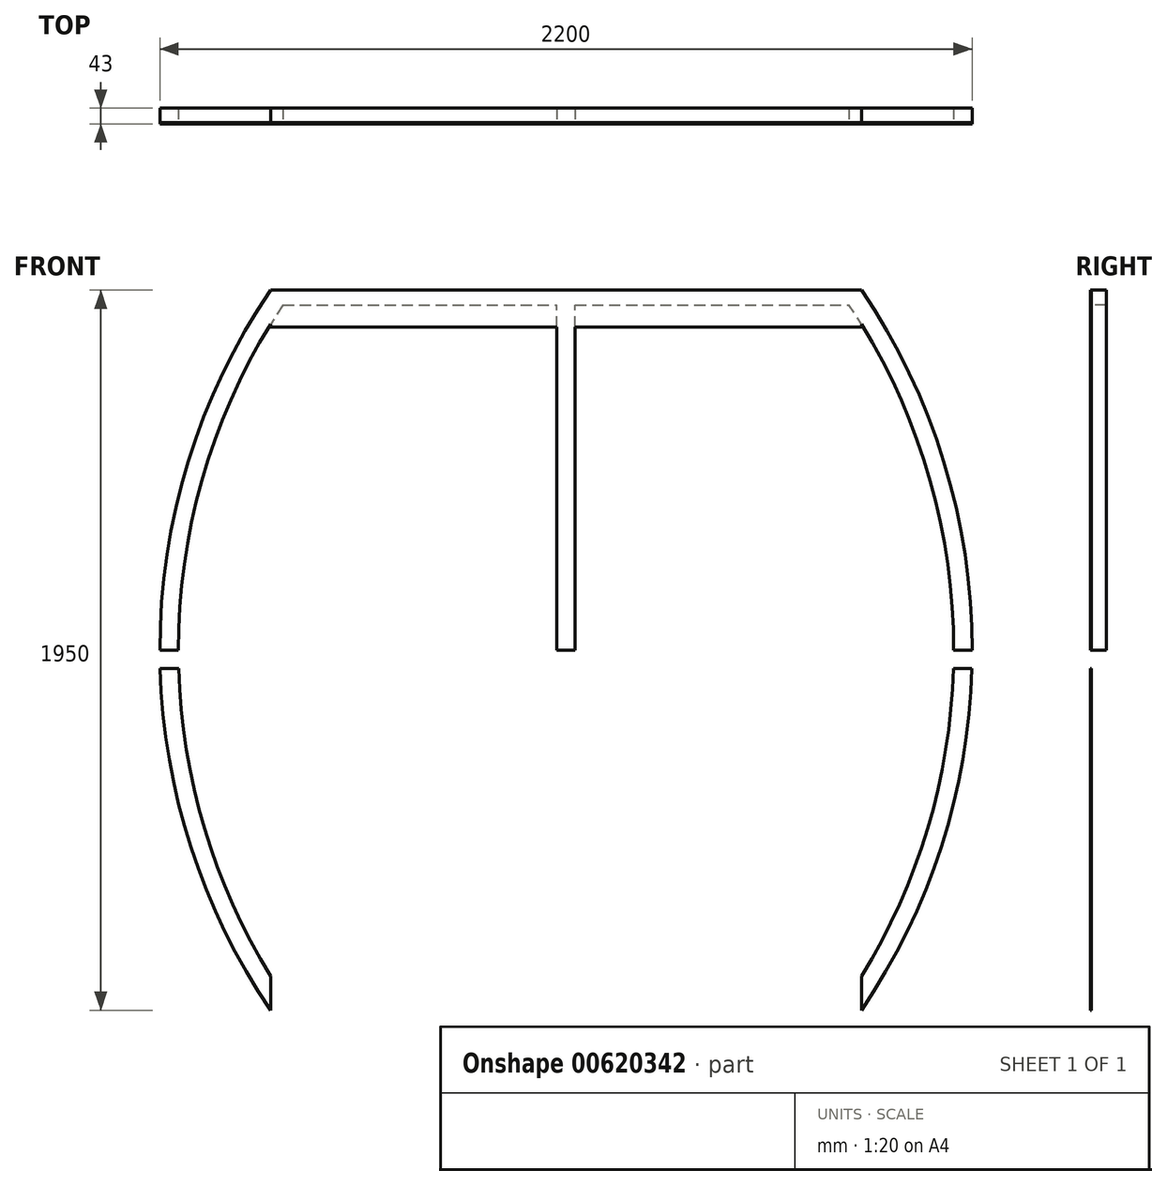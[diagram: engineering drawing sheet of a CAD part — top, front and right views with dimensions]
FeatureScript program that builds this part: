
annotation { "Feature Type Name" : "Feature", "Feature Type Description" : "" }
export const myFeature = defineFeature(function(context is Context, id is Id, definition is map)
    precondition{}
    {
        {
            var Q0;
            Q0=qCreatedBy(makeId("Front.planeOp"),FACE);
            var sketch = newSketch(context, id + "F0", { "sketchPlane" : qUnion([Q0])});
            skLineSegment(sketch, "E0.bottom", {"start": v(-800, 1950) * mm, "end": v(800, 1950) * mm});
            skLineSegment(sketch, "E0.top", {"start": v(-800, 0) * mm, "end": v(800, 0) * mm});
            skLineSegment(sketch, "E0.left", {"start": v(-800, 1950) * mm, "end": v(-800, 0) * mm});
            skLineSegment(sketch, "E0.right", {"start": v(800, 1950) * mm, "end": v(800, 0) * mm});
            skArc(sketch, "E1", {"start": v(800, 0) * mm, "mid": v(1100, 975) * mm, "end": v(800, 1950) * mm});
            skArc(sketch, "E2", {"start": v(-800, 1950) * mm, "mid": v(-1100, 975) * mm, "end": v(-800, 0) * mm});
            skArc(sketch, "E3", {"start": v(-766.66, 1910) * mm, "mid": v(-1049.99, 981) * mm, "end": v(-773.28, 50) * mm});
            skArc(sketch, "E4", {"start": v(773.28, 50) * mm, "mid": v(1049.99, 981) * mm, "end": v(766.66, 1910) * mm});
            skLineSegment(sketch, "E5", {"start": v(-1050, 975) * mm, "end": v(1050, 975) * mm});
            skPoint(sketch, "E5.startSnap0", {"position": v(-1100, 975) * mm});
            skLineSegment(sketch, "E6", {"start": v(-804.9, 1850) * mm, "end": v(804.9, 1850) * mm});
            skLineSegment(sketch, "E7", {"start": v(-773.28, 50) * mm, "end": v(773.28, 50) * mm});
            skLineSegment(sketch, "E8", {"start": v(0, 1950) * mm, "end": v(0, 975) * mm});
            skLineSegment(sketch, "E9", {"start": v(-25, 1850) * mm, "end": v(-25, 975) * mm});
            skLineSegment(sketch, "E10", {"start": v(-25, 975) * mm, "end": v(25, 975) * mm});
            skLineSegment(sketch, "E11", {"start": v(25, 975) * mm, "end": v(25, 1850) * mm});
            skLineSegment(sketch, "E12", {"start": v(-1099.28, 925) * mm, "end": v(1099.28, 925) * mm});
            skLineSegment(sketch, "E13", {"start": v(-25, 975) * mm, "end": v(-25, 925) * mm});
            skLineSegment(sketch, "E14", {"start": v(25, 975) * mm, "end": v(25, 925) * mm});
            skLineSegment(sketch, "E15", {"start": v(-750, 0) * mm, "end": v(-750, 50) * mm});
            skLineSegment(sketch, "E16", {"start": v(-750, 50) * mm, "end": v(-650, 50) * mm});
            skLineSegment(sketch, "E17", {"start": v(-650, 50) * mm, "end": v(-650, 0) * mm});
            skLineSegment(sketch, "E18", {"start": v(-50, 0) * mm, "end": v(-50, 50) * mm});
            skLineSegment(sketch, "E19", {"start": v(-50, 50) * mm, "end": v(50, 50) * mm});
            skLineSegment(sketch, "E20", {"start": v(50, 50) * mm, "end": v(50, 0) * mm});
            skLineSegment(sketch, "E21", {"start": v(650, 0) * mm, "end": v(650, 50) * mm});
            skLineSegment(sketch, "E22", {"start": v(650, 50) * mm, "end": v(750, 50) * mm});
            skLineSegment(sketch, "E23", {"start": v(750, 50) * mm, "end": v(750, 0) * mm});
            skLineSegment(sketch, "E24", {"start": v(0, 50) * mm, "end": v(0, 0) * mm});
            skLineSegment(sketch, "E25", {"start": v(-800, 1910) * mm, "end": v(800, 1910) * mm});
            skLineSegment(sketch, "E26", {"start": v(-1050, 975) * mm, "end": v(-1100, 975) * mm});
            skLineSegment(sketch, "E27", {"start": v(1050, 975) * mm, "end": v(1100, 975) * mm});
            skLineSegment(sketch, "E28", {"start": v(25, 1850) * mm, "end": v(25, 1910) * mm});
            skLineSegment(sketch, "E29", {"start": v(-25, 1850) * mm, "end": v(-25, 1910) * mm});
            skSolve(sketch);
        }
        {
            var Q0;
            {var subQ4=sQuery(id+"F0.wireOp",EDGE,"E25");var subQ6=sQuery(id+"F0.wireOp",EDGE,"E0.left");var subQ8=makeQuery(id+"F0.imprint","INTERSECT",VERTEX,{"derivedFrom":[subQ6,subQ4]});Q0=makeQuery(id+"F0.imprint","IMPRINT",FACE,{"disambiguationData":[TD([[makeQuery(id+"F0.imprint","IMPRINT",EDGE,{"disambiguationData":[TD([[subQ8,-1.0]])],"derivedFrom":subQ6}),1.0]])]});}
            var Q1;
            {var subQ1=sQuery(id+"F0.wireOp",EDGE,"E0.bottom");var subQ3=sQuery(id+"F0.wireOp",EDGE,"E8");var subQ4=makeQuery(id+"F0.imprint","INTERSECT",VERTEX,{"derivedFrom":[subQ1,subQ3]});Q1=makeQuery(id+"F0.imprint","IMPRINT",FACE,{"disambiguationData":[TD([[makeQuery(id+"F0.imprint","IMPRINT",EDGE,{"disambiguationData":[TD([[subQ4,-1.0]])],"derivedFrom":subQ3}),-1.0]])]});}
            var Q2;
            {var subQ1=sQuery(id+"F0.wireOp",EDGE,"E0.bottom");var subQ3=sQuery(id+"F0.wireOp",EDGE,"E8");var subQ4=makeQuery(id+"F0.imprint","INTERSECT",VERTEX,{"derivedFrom":[subQ1,subQ3]});Q2=makeQuery(id+"F0.imprint","IMPRINT",FACE,{"disambiguationData":[TD([[makeQuery(id+"F0.imprint","IMPRINT",EDGE,{"disambiguationData":[TD([[subQ4,-1.0]])],"derivedFrom":subQ3}),1.0]])]});}
            var Q3;
            {var subQ3=sQuery(id+"F0.wireOp",EDGE,"E25");var subQ6=sQuery(id+"F0.wireOp",EDGE,"E0.right");var subQ8=makeQuery(id+"F0.imprint","INTERSECT",VERTEX,{"derivedFrom":[subQ6,subQ3]});Q3=makeQuery(id+"F0.imprint","IMPRINT",FACE,{"disambiguationData":[TD([[makeQuery(id+"F0.imprint","IMPRINT",EDGE,{"disambiguationData":[TD([[subQ8,-1.0]])],"derivedFrom":subQ6}),-1.0]])]});}
            var Q4;
            {var subQ0=sQuery(id+"F0.wireOp",EDGE,"E29");Q4=makeQuery(id+"F0.imprint","IMPRINT",FACE,{"disambiguationData":[TD([[makeQuery(id+"F0.imprint","IMPRINT",EDGE,{"derivedFrom":subQ0}),-1.0]])]});}
            var Q5;
            {var subQ0=sQuery(id+"F0.wireOp",EDGE,"E28");Q5=makeQuery(id+"F0.imprint","IMPRINT",FACE,{"disambiguationData":[TD([[makeQuery(id+"F0.imprint","IMPRINT",EDGE,{"derivedFrom":subQ0}),1.0]])]});}
            var Q6;
            {var subQ3=sQuery(id+"F0.wireOp",EDGE,"E29");Q6=makeQuery(id+"F0.imprint","IMPRINT",FACE,{"disambiguationData":[TD([[makeQuery(id+"F0.imprint","IMPRINT",EDGE,{"derivedFrom":subQ3}),1.0]])]});}
            var Q7;
            {var subQ3=sQuery(id+"F0.wireOp",EDGE,"E28");Q7=makeQuery(id+"F0.imprint","IMPRINT",FACE,{"disambiguationData":[TD([[makeQuery(id+"F0.imprint","IMPRINT",EDGE,{"derivedFrom":subQ3}),-1.0]])]});}
            extrude(context, id + "F1", {"entities" : qUnion([Q0, Q1, Q2, Q3, Q4, Q5, Q6, Q7]), "depth" : 3 * mm, "offsetDistance" : 25 * mm});
        }
        {
            var Q0;
            {var subQ3=sQuery(id+"F0.wireOp",EDGE,"E26");Q0=makeQuery(id+"F0.imprint","IMPRINT",FACE,{"disambiguationData":[TD([[makeQuery(id+"F0.imprint","IMPRINT",EDGE,{"derivedFrom":subQ3}),-1.0]])]});}
            var Q1;
            {var subQ0=sQuery(id+"F0.wireOp",EDGE,"E3");var subQ1=sQuery(id+"F0.wireOp",EDGE,"E0.left");var subQ2=makeQuery(id+"F0.imprint","INTERSECT",VERTEX,{"disambiguationData":[OD(0.0)],"derivedFrom":[subQ1,subQ0]});Q1=makeQuery(id+"F0.imprint","IMPRINT",FACE,{"disambiguationData":[TD([[makeQuery(id+"F0.imprint","IMPRINT",EDGE,{"disambiguationData":[TD([[subQ2,-1.0]])],"derivedFrom":subQ1}),-1.0]])]});}
            extrude(context, id + "F2", {"entities" : qUnion([Q0, Q1]), "operationType" : NewBodyOperationType.ADD, "depth" : 3 * mm, "offsetDistance" : 25 * mm});
        }
        {
            var Q0;
            {var subQ0=sQuery(id+"F0.wireOp",EDGE,"E9");Q0=makeQuery(id+"F0.imprint","IMPRINT",FACE,{"disambiguationData":[TD([[makeQuery(id+"F0.imprint","IMPRINT",EDGE,{"derivedFrom":subQ0}),1.0]])]});}
            var Q1;
            {var subQ0=sQuery(id+"F0.wireOp",EDGE,"E11");Q1=makeQuery(id+"F0.imprint","IMPRINT",FACE,{"disambiguationData":[TD([[makeQuery(id+"F0.imprint","IMPRINT",EDGE,{"derivedFrom":subQ0}),1.0]])]});}
            extrude(context, id + "F3", {"entities" : qUnion([Q0, Q1]), "operationType" : NewBodyOperationType.ADD, "depth" : 3 * mm, "offsetDistance" : 25 * mm});
        }
        {
            var Q0;
            {var subQ3=sQuery(id+"F0.wireOp",EDGE,"E27");Q0=makeQuery(id+"F0.imprint","IMPRINT",FACE,{"disambiguationData":[TD([[makeQuery(id+"F0.imprint","IMPRINT",EDGE,{"derivedFrom":subQ3}),1.0]])]});}
            var Q1;
            {var subQ0=sQuery(id+"F0.wireOp",EDGE,"E4");var subQ1=sQuery(id+"F0.wireOp",EDGE,"E0.right");var subQ2=makeQuery(id+"F0.imprint","INTERSECT",VERTEX,{"disambiguationData":[OD(0.0)],"derivedFrom":[subQ1,subQ0]});Q1=makeQuery(id+"F0.imprint","IMPRINT",FACE,{"disambiguationData":[TD([[makeQuery(id+"F0.imprint","IMPRINT",EDGE,{"disambiguationData":[TD([[subQ2,-1.0]])],"derivedFrom":subQ1}),1.0]])]});}
            extrude(context, id + "F4", {"entities" : qUnion([Q0, Q1]), "operationType" : NewBodyOperationType.ADD, "depth" : 3 * mm, "offsetDistance" : 25 * mm});
        }
        {
            var Q0;
            {var subQ4=sQuery(id+"F0.wireOp",EDGE,"E0.bottom");var subQ6=sQuery(id+"F0.wireOp",EDGE,"E8");var subQ7=makeQuery(id+"F0.imprint","INTERSECT",VERTEX,{"derivedFrom":[subQ4,subQ6]});Q0=makeQuery(id+"F0.imprint","IMPRINT",FACE,{"disambiguationData":[TD([[makeQuery(id+"F0.imprint","IMPRINT",EDGE,{"disambiguationData":[TD([[subQ7,-1.0]])],"derivedFrom":subQ6}),-1.0]])]});}
            var Q1;
            {var subQ0=sQuery(id+"F0.wireOp",EDGE,"E28");Q1=makeQuery(id+"F0.imprint","IMPRINT",FACE,{"disambiguationData":[TD([[makeQuery(id+"F0.imprint","IMPRINT",EDGE,{"derivedFrom":subQ0}),1.0]])]});}
            var Q2;
            {var subQ0=sQuery(id+"F0.wireOp",EDGE,"E29");Q2=makeQuery(id+"F0.imprint","IMPRINT",FACE,{"disambiguationData":[TD([[makeQuery(id+"F0.imprint","IMPRINT",EDGE,{"derivedFrom":subQ0}),-1.0]])]});}
            var Q3;
            {var subQ0=sQuery(id+"F0.wireOp",EDGE,"E9");Q3=makeQuery(id+"F0.imprint","IMPRINT",FACE,{"disambiguationData":[TD([[makeQuery(id+"F0.imprint","IMPRINT",EDGE,{"derivedFrom":subQ0}),1.0]])]});}
            var Q4;
            {var subQ0=sQuery(id+"F0.wireOp",EDGE,"E11");Q4=makeQuery(id+"F0.imprint","IMPRINT",FACE,{"disambiguationData":[TD([[makeQuery(id+"F0.imprint","IMPRINT",EDGE,{"derivedFrom":subQ0}),1.0]])]});}
            var Q5;
            {var subQ3=sQuery(id+"F0.wireOp",EDGE,"E27");Q5=makeQuery(id+"F0.imprint","IMPRINT",FACE,{"disambiguationData":[TD([[makeQuery(id+"F0.imprint","IMPRINT",EDGE,{"derivedFrom":subQ3}),1.0]])]});}
            var Q6;
            {var subQ3=sQuery(id+"F0.wireOp",EDGE,"E26");Q6=makeQuery(id+"F0.imprint","IMPRINT",FACE,{"disambiguationData":[TD([[makeQuery(id+"F0.imprint","IMPRINT",EDGE,{"derivedFrom":subQ3}),-1.0]])]});}
            var Q7;
            {var subQ2=sQuery(id+"F0.wireOp",EDGE,"E8");var subQ4=sQuery(id+"F0.wireOp",EDGE,"E0.bottom");var subQ5=makeQuery(id+"F0.imprint","INTERSECT",VERTEX,{"derivedFrom":[subQ4,subQ2]});Q7=makeQuery(id+"F0.imprint","IMPRINT",FACE,{"disambiguationData":[TD([[makeQuery(id+"F0.imprint","IMPRINT",EDGE,{"disambiguationData":[TD([[subQ5,-1.0]])],"derivedFrom":subQ2}),1.0]])]});}
            var Q8;
            {var subQ0=sQuery(id+"F0.wireOp",EDGE,"E25");var subQ1=sQuery(id+"F0.wireOp",EDGE,"E0.right");var subQ2=makeQuery(id+"F0.imprint","INTERSECT",VERTEX,{"derivedFrom":[subQ1,subQ0]});Q8=makeQuery(id+"F0.imprint","IMPRINT",FACE,{"disambiguationData":[TD([[makeQuery(id+"F0.imprint","IMPRINT",EDGE,{"disambiguationData":[TD([[subQ2,-1.0]])],"derivedFrom":subQ1}),-1.0]])]});}
            var Q9;
            {var subQ0=sQuery(id+"F0.wireOp",EDGE,"E25");var subQ1=sQuery(id+"F0.wireOp",EDGE,"E0.left");var subQ2=makeQuery(id+"F0.imprint","INTERSECT",VERTEX,{"derivedFrom":[subQ1,subQ0]});Q9=makeQuery(id+"F0.imprint","IMPRINT",FACE,{"disambiguationData":[TD([[makeQuery(id+"F0.imprint","IMPRINT",EDGE,{"disambiguationData":[TD([[subQ2,-1.0]])],"derivedFrom":subQ1}),1.0]])]});}
            extrude(context, id + "F5", {"entities" : qUnion([Q0, Q1, Q2, Q3, Q4, Q5, Q6, Q7, Q8, Q9]), "oppositeDirection" : true, "depth" : 40 * mm, "offsetDistance" : 25 * mm});
        }
    });
